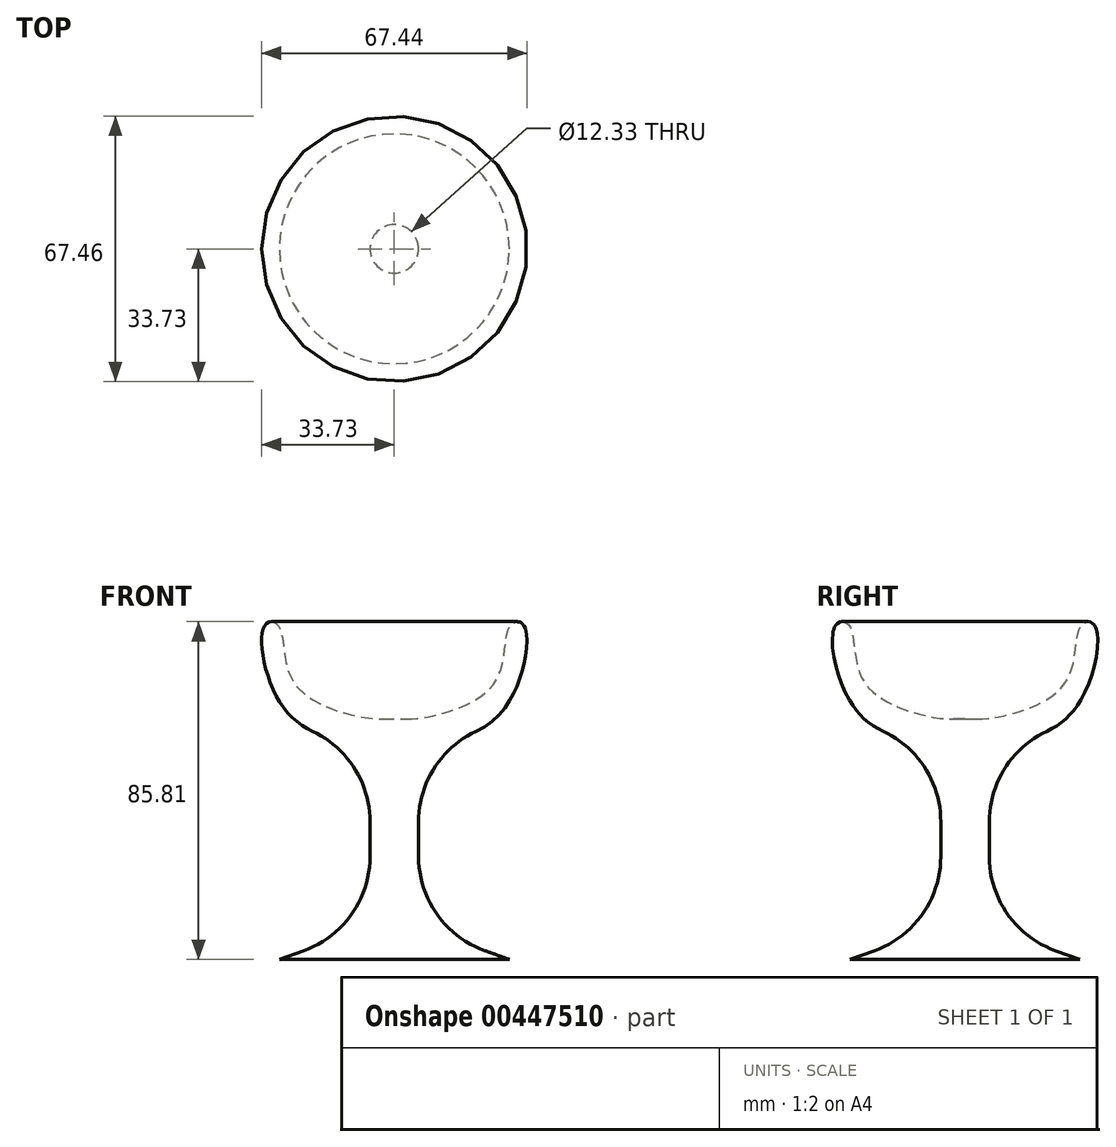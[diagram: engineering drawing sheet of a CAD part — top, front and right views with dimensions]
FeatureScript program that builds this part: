
annotation { "Feature Type Name" : "Feature", "Feature Type Description" : "" }
export const myFeature = defineFeature(function(context is Context, id is Id, definition is map)
    precondition{}
    {
        {
            var Q0;
            Q0=qCreatedBy(makeId("Front.planeOp"),FACE);
            var sketch = newSketch(context, id + "F0", { "sketchPlane" : qUnion([Q0])});
            skLineSegment(sketch, "E0", {"start": v(0, 0) * mm, "end": v(0, 84.92) * mm, "construction": true});
            skLineSegment(sketch, "E1", {"start": v(0, 0) * mm, "end": v(-29.2, 0) * mm});
            skLineSegment(sketch, "E2", {"start": v(-29.2, 0) * mm, "end": v(-6.17, 8.24) * mm});
            skLineSegment(sketch, "E3", {"start": v(-6.17, 8.24) * mm, "end": v(-6.17, 54.56) * mm});
            skFitSpline(sketch, "E4", {"points": [v(-6.17, 54.56) * mm, v(-27.69, 63.39) * mm, v(-32.86, 84.92) * mm, v(-29.51, 84.92) * mm, v(-25.56, 70.38) * mm, v(-6.17, 61.26) * mm, v(0, 61.26) * mm], "startDerivative": vector(-113.24, 14.91) * mm, "endDerivative": vector(43.6, 4.95) * mm});
            skSolve(sketch);
        }
        {
            var Q0;
            Q0=sQuery(id+"F0.wireOp",EDGE,"E4");
            var Q1;
            Q1=sQuery(id+"F0.wireOp",EDGE,"E3");
            var Q2;
            Q2=sQuery(id+"F0.wireOp",EDGE,"E2");
            var Q3;
            Q3=sQuery(id+"F0.wireOp",EDGE,"E1");
            var Q4;
            Q4=sQuery(id+"F0.wireOp",EDGE,"E0");
            revolve(context, id + "F1", {"bodyType" : ToolBodyType.SURFACE, "surfaceEntities" : qUnion([Q0, Q1, Q2, Q3]), "axis" : qUnion([Q4]), "revolveType" : RevolveType.FULL});
        }
        {
            var Q0;
            Q0=makeQuery(id+"F1.opRevolve","SWEPT_EDGE",EDGE,{"disambiguationData":[OSD([sQuery(id+"F0.wireOp",VERTEX,"E2.end")])]});
            var Q1;
            Q1=makeQuery(id+"F1.opRevolve","SWEPT_EDGE",EDGE,{"disambiguationData":[OSD([sQuery(id+"F0.wireOp",VERTEX,"E3.end")])]});
            fillet(context, id + "F2", {"entities" : qUnion([Q0, Q1]), "radius" : 25.4 * mm, "tangentPropagation" : true, "allowEdgeOverflow" : false});
        }
    });
